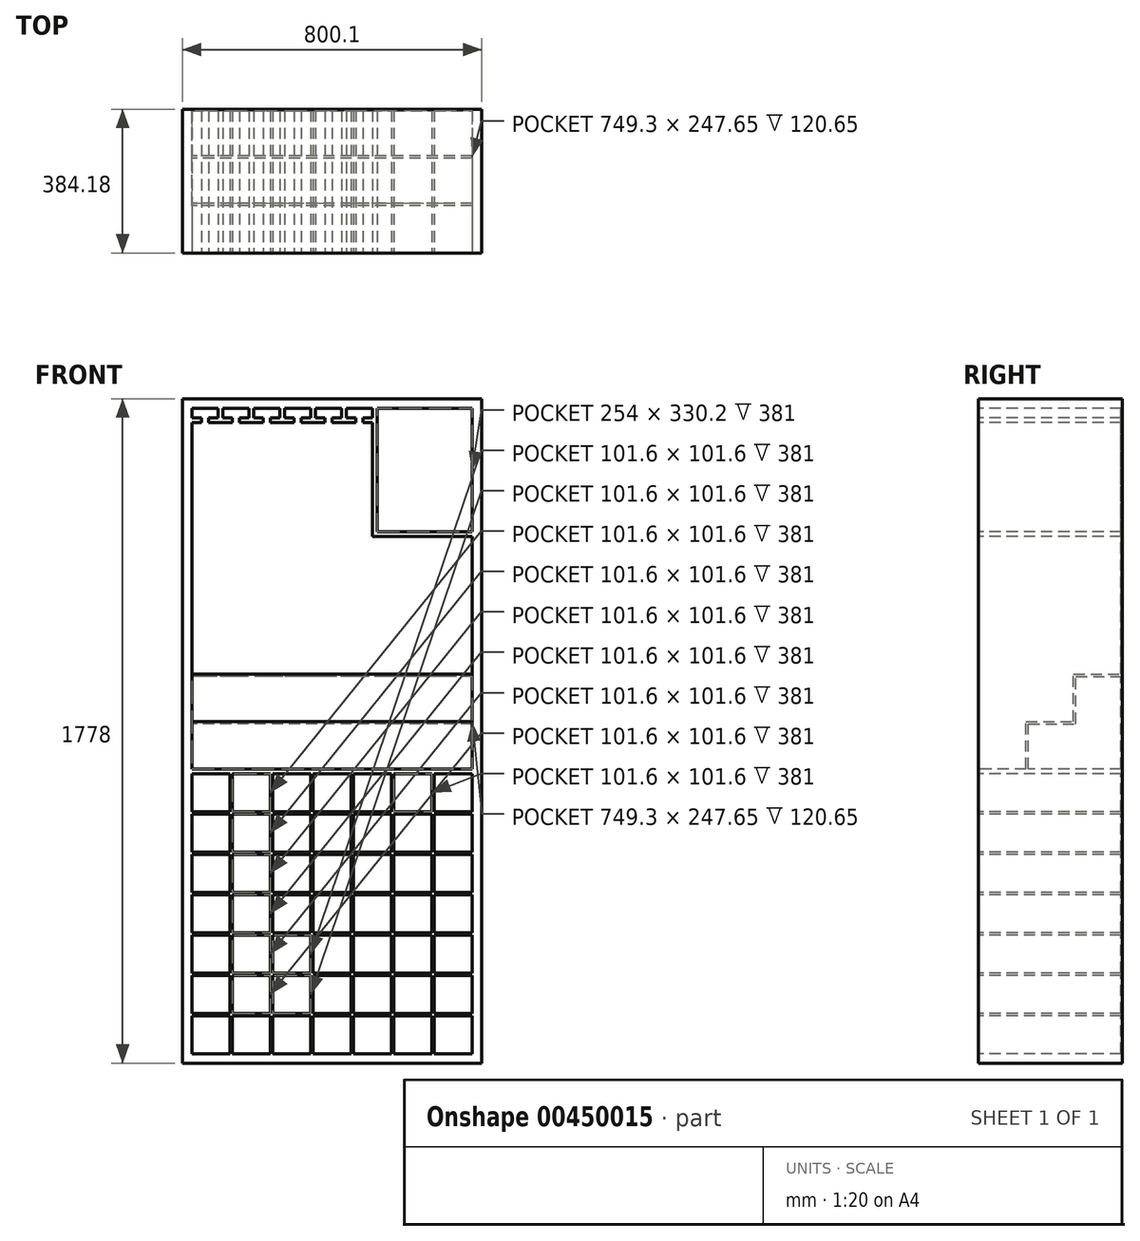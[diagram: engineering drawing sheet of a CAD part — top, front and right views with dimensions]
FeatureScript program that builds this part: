
annotation { "Feature Type Name" : "Feature", "Feature Type Description" : "" }
export const myFeature = defineFeature(function(context is Context, id is Id, definition is map)
    precondition{}
    {
        {
            var Q0;
            Q0=qCreatedBy(makeId("Front.planeOp"),FACE);
            var sketch = newSketch(context, id + "F0", { "sketchPlane" : qUnion([Q0])});
            skLineSegment(sketch, "E0", {"start": v(-400.05, 0) * mm, "end": v(400.05, 0) * mm});
            skLineSegment(sketch, "E1", {"start": v(-400.05, 0) * mm, "end": v(-400.05, 1778) * mm});
            skLineSegment(sketch, "E2", {"start": v(-400.05, 1778) * mm, "end": v(400.05, 1778) * mm});
            skLineSegment(sketch, "E3", {"start": v(400.05, 1778) * mm, "end": v(400.05, 0) * mm});
            skLineSegment(sketch, "E4.0", {"start": v(-374.65, 1752.6) * mm, "end": v(374.65, 1752.6) * mm});
            skLineSegment(sketch, "E5.0", {"start": v(-374.65, 25.4) * mm, "end": v(-374.65, 1752.6) * mm});
            skLineSegment(sketch, "E5.1", {"start": v(-374.65, 25.4) * mm, "end": v(374.65, 25.4) * mm});
            skLineSegment(sketch, "E5.2", {"start": v(374.65, 1752.6) * mm, "end": v(374.65, 25.4) * mm});
            skSolve(sketch);
        }
        {
            var Q0;
            Q0 = qSketchRegion(id + "F0", true);
            extrude(context, id + "F1", {"entities" : qUnion([Q0]), "oppositeDirection" : true, "depth" : 381 * mm});
        }
        {
            var Q0;
            Q0=makeQuery(id+"F1.opExtrude","CAP_FACE",FACE,{"disambiguationData":[OSD([sQuery(id+"F0.wireOp",EDGE,"E0"),sQuery(id+"F0.wireOp",EDGE,"E1"),sQuery(id+"F0.wireOp",EDGE,"E2"),sQuery(id+"F0.wireOp",EDGE,"E3"),sQuery(id+"F0.wireOp",EDGE,"E4.0"),sQuery(id+"F0.wireOp",EDGE,"E5.0"),sQuery(id+"F0.wireOp",EDGE,"E5.1"),sQuery(id+"F0.wireOp",EDGE,"E5.2")])],"isStart":false});
            var sketch = newSketch(context, id + "F2", { "sketchPlane" : qUnion([Q0])});
            skLineSegment(sketch, "E6.0", {"start": v(400.05, 1778) * mm, "end": v(-400.05, 1778) * mm});
            skLineSegment(sketch, "E6.1", {"start": v(-400.05, 1778) * mm, "end": v(-400.05, 0) * mm});
            skLineSegment(sketch, "E6.2", {"start": v(400.05, 0) * mm, "end": v(400.05, 1778) * mm});
            skLineSegment(sketch, "E7.0", {"start": v(400.05, 0) * mm, "end": v(-400.05, 0) * mm});
            skSolve(sketch);
        }
        {
            var Q0;
            Q0 = qSketchRegion(id + "F2", true);
            extrude(context, id + "F3", {"entities" : qUnion([Q0]), "operationType" : NewBodyOperationType.ADD, "depth" : 3.17 * mm});
        }
        {
            var Q0;
            Q0=makeQuery(id+"F1.opExtrude","CAP_FACE",FACE,{"disambiguationData":[OSD([sQuery(id+"F0.wireOp",EDGE,"E0"),sQuery(id+"F0.wireOp",EDGE,"E1"),sQuery(id+"F0.wireOp",EDGE,"E2"),sQuery(id+"F0.wireOp",EDGE,"E3"),sQuery(id+"F0.wireOp",EDGE,"E4.0"),sQuery(id+"F0.wireOp",EDGE,"E5.0"),sQuery(id+"F0.wireOp",EDGE,"E5.1"),sQuery(id+"F0.wireOp",EDGE,"E5.2")])],"isStart":true});
            var sketch = newSketch(context, id + "F4", { "sketchPlane" : qUnion([Q0])});
            skLineSegment(sketch, "E8", {"start": v(-374.65, 889) * mm, "end": v(374.65, 889) * mm, "construction": true});
            skLineSegment(sketch, "E9", {"start": v(-374.65, 774.7) * mm, "end": v(374.65, 774.7) * mm});
            skLineSegment(sketch, "E10", {"start": v(-374.65, 774.7) * mm, "end": v(-374.65, 25.4) * mm});
            skLineSegment(sketch, "E11", {"start": v(-374.65, 25.4) * mm, "end": v(374.65, 25.4) * mm});
            skLineSegment(sketch, "E12", {"start": v(374.65, 25.4) * mm, "end": v(374.65, 774.7) * mm});
            skLineSegment(sketch, "E13", {"start": v(-266.7, 774.7) * mm, "end": v(-266.7, 25.4) * mm});
            skLineSegment(sketch, "E14.0", {"start": v(-273.05, 774.7) * mm, "end": v(-273.05, 25.4) * mm});
            skLineSegment(sketch, "E15.1.0.0", {"start": v(-165.1, 774.7) * mm, "end": v(-165.1, 25.4) * mm});
            skLineSegment(sketch, "E15.1.0.1", {"start": v(-158.75, 774.7) * mm, "end": v(-158.75, 25.4) * mm});
            skLineSegment(sketch, "E15.2.0.0", {"start": v(-57.15, 774.7) * mm, "end": v(-57.15, 25.4) * mm});
            skLineSegment(sketch, "E15.2.0.1", {"start": v(-50.8, 774.7) * mm, "end": v(-50.8, 25.4) * mm});
            skLineSegment(sketch, "E15.3.0.0", {"start": v(50.8, 774.7) * mm, "end": v(50.8, 25.4) * mm});
            skLineSegment(sketch, "E15.3.0.1", {"start": v(57.15, 774.7) * mm, "end": v(57.15, 25.4) * mm});
            skLineSegment(sketch, "E15.4.0.0", {"start": v(158.75, 774.7) * mm, "end": v(158.75, 25.4) * mm});
            skLineSegment(sketch, "E15.4.0.1", {"start": v(165.1, 774.7) * mm, "end": v(165.1, 25.4) * mm});
            skLineSegment(sketch, "E15.5.0.0", {"start": v(266.7, 774.7) * mm, "end": v(266.7, 25.4) * mm});
            skLineSegment(sketch, "E15.5.0.1", {"start": v(273.05, 774.7) * mm, "end": v(273.05, 25.4) * mm});
            skLineSegment(sketch, "E15.direction1", {"start": v(-273.05, 25.4) * mm, "end": v(-165.1, 25.4) * mm, "construction": true});
            skLineSegment(sketch, "E16", {"start": v(-374.65, 127) * mm, "end": v(-273.05, 127) * mm});
            skLineSegment(sketch, "E17", {"start": v(-266.7, 127) * mm, "end": v(-165.1, 127) * mm});
            skLineSegment(sketch, "E18.trimOffspring", {"start": v(-158.75, 127) * mm, "end": v(-57.15, 127) * mm});
            skLineSegment(sketch, "E19.trimOffspring", {"start": v(-50.8, 127) * mm, "end": v(50.8, 127) * mm});
            skLineSegment(sketch, "E20.trimOffspring", {"start": v(57.15, 127) * mm, "end": v(158.75, 127) * mm});
            skLineSegment(sketch, "E21.trimOffspring", {"start": v(165.1, 127) * mm, "end": v(266.7, 127) * mm});
            skLineSegment(sketch, "E22.trimOffspring", {"start": v(273.05, 127) * mm, "end": v(374.65, 127) * mm});
            skLineSegment(sketch, "E23", {"start": v(-374.65, 133.35) * mm, "end": v(-273.05, 133.35) * mm});
            skLineSegment(sketch, "E24.trimOffspring", {"start": v(-266.7, 133.35) * mm, "end": v(-165.1, 133.35) * mm});
            skLineSegment(sketch, "E25.trimOffspring", {"start": v(-158.75, 133.35) * mm, "end": v(-57.15, 133.35) * mm});
            skLineSegment(sketch, "E26.trimOffspring", {"start": v(-50.8, 133.35) * mm, "end": v(50.8, 133.35) * mm});
            skLineSegment(sketch, "E27.trimOffspring", {"start": v(57.15, 133.35) * mm, "end": v(158.75, 133.35) * mm});
            skLineSegment(sketch, "E28.trimOffspring", {"start": v(165.1, 133.35) * mm, "end": v(266.7, 133.35) * mm});
            skLineSegment(sketch, "E29.trimOffspring", {"start": v(273.05, 133.35) * mm, "end": v(374.65, 133.35) * mm});
            skLineSegment(sketch, "E30.0.1.0", {"start": v(-374.65, 241.3) * mm, "end": v(-273.05, 241.3) * mm});
            skLineSegment(sketch, "E30.0.1.1", {"start": v(-374.65, 234.95) * mm, "end": v(-273.05, 234.95) * mm});
            skLineSegment(sketch, "E30.0.1.2", {"start": v(-266.7, 234.95) * mm, "end": v(-165.1, 234.95) * mm});
            skLineSegment(sketch, "E30.0.1.3", {"start": v(-266.7, 241.3) * mm, "end": v(-165.1, 241.3) * mm});
            skLineSegment(sketch, "E30.0.1.4", {"start": v(-158.75, 241.3) * mm, "end": v(-57.15, 241.3) * mm});
            skLineSegment(sketch, "E30.0.1.5", {"start": v(-158.75, 234.95) * mm, "end": v(-57.15, 234.95) * mm});
            skLineSegment(sketch, "E30.0.1.6", {"start": v(-50.8, 234.95) * mm, "end": v(50.8, 234.95) * mm});
            skLineSegment(sketch, "E30.0.1.7", {"start": v(-50.8, 241.3) * mm, "end": v(50.8, 241.3) * mm});
            skLineSegment(sketch, "E30.0.1.8", {"start": v(57.15, 241.3) * mm, "end": v(158.75, 241.3) * mm});
            skLineSegment(sketch, "E30.0.1.9", {"start": v(57.15, 234.95) * mm, "end": v(158.75, 234.95) * mm});
            skLineSegment(sketch, "E30.0.1.10", {"start": v(165.1, 234.95) * mm, "end": v(266.7, 234.95) * mm});
            skLineSegment(sketch, "E30.0.1.11", {"start": v(165.1, 241.3) * mm, "end": v(266.7, 241.3) * mm});
            skLineSegment(sketch, "E30.0.1.12", {"start": v(273.05, 241.3) * mm, "end": v(374.65, 241.3) * mm});
            skLineSegment(sketch, "E30.0.1.13", {"start": v(273.05, 234.95) * mm, "end": v(374.65, 234.95) * mm});
            skLineSegment(sketch, "E30.0.2.0", {"start": v(-374.65, 349.25) * mm, "end": v(-273.05, 349.25) * mm});
            skLineSegment(sketch, "E30.0.2.1", {"start": v(-374.65, 342.9) * mm, "end": v(-273.05, 342.9) * mm});
            skLineSegment(sketch, "E30.0.2.2", {"start": v(-266.7, 342.9) * mm, "end": v(-165.1, 342.9) * mm});
            skLineSegment(sketch, "E30.0.2.3", {"start": v(-266.7, 349.25) * mm, "end": v(-165.1, 349.25) * mm});
            skLineSegment(sketch, "E30.0.2.4", {"start": v(-158.75, 349.25) * mm, "end": v(-57.15, 349.25) * mm});
            skLineSegment(sketch, "E30.0.2.5", {"start": v(-158.75, 342.9) * mm, "end": v(-57.15, 342.9) * mm});
            skLineSegment(sketch, "E30.0.2.6", {"start": v(-50.8, 342.9) * mm, "end": v(50.8, 342.9) * mm});
            skLineSegment(sketch, "E30.0.2.7", {"start": v(-50.8, 349.25) * mm, "end": v(50.8, 349.25) * mm});
            skLineSegment(sketch, "E30.0.2.8", {"start": v(57.15, 349.25) * mm, "end": v(158.75, 349.25) * mm});
            skLineSegment(sketch, "E30.0.2.9", {"start": v(57.15, 342.9) * mm, "end": v(158.75, 342.9) * mm});
            skLineSegment(sketch, "E30.0.2.10", {"start": v(165.1, 342.9) * mm, "end": v(266.7, 342.9) * mm});
            skLineSegment(sketch, "E30.0.2.11", {"start": v(165.1, 349.25) * mm, "end": v(266.7, 349.25) * mm});
            skLineSegment(sketch, "E30.0.2.12", {"start": v(273.05, 349.25) * mm, "end": v(374.65, 349.25) * mm});
            skLineSegment(sketch, "E30.0.2.13", {"start": v(273.05, 342.9) * mm, "end": v(374.65, 342.9) * mm});
            skLineSegment(sketch, "E30.0.3.0", {"start": v(-374.65, 457.2) * mm, "end": v(-273.05, 457.2) * mm});
            skLineSegment(sketch, "E30.0.3.1", {"start": v(-374.65, 450.85) * mm, "end": v(-273.05, 450.85) * mm});
            skLineSegment(sketch, "E30.0.3.2", {"start": v(-266.7, 450.85) * mm, "end": v(-165.1, 450.85) * mm});
            skLineSegment(sketch, "E30.0.3.3", {"start": v(-266.7, 457.2) * mm, "end": v(-165.1, 457.2) * mm});
            skLineSegment(sketch, "E30.0.3.4", {"start": v(-158.75, 457.2) * mm, "end": v(-57.15, 457.2) * mm});
            skLineSegment(sketch, "E30.0.3.5", {"start": v(-158.75, 450.85) * mm, "end": v(-57.15, 450.85) * mm});
            skLineSegment(sketch, "E30.0.3.6", {"start": v(-50.8, 450.85) * mm, "end": v(50.8, 450.85) * mm});
            skLineSegment(sketch, "E30.0.3.7", {"start": v(-50.8, 457.2) * mm, "end": v(50.8, 457.2) * mm});
            skLineSegment(sketch, "E30.0.3.8", {"start": v(57.15, 457.2) * mm, "end": v(158.75, 457.2) * mm});
            skLineSegment(sketch, "E30.0.3.9", {"start": v(57.15, 450.85) * mm, "end": v(158.75, 450.85) * mm});
            skLineSegment(sketch, "E30.0.3.10", {"start": v(165.1, 450.85) * mm, "end": v(266.7, 450.85) * mm});
            skLineSegment(sketch, "E30.0.3.11", {"start": v(165.1, 457.2) * mm, "end": v(266.7, 457.2) * mm});
            skLineSegment(sketch, "E30.0.3.12", {"start": v(273.05, 457.2) * mm, "end": v(374.65, 457.2) * mm});
            skLineSegment(sketch, "E30.0.3.13", {"start": v(273.05, 450.85) * mm, "end": v(374.65, 450.85) * mm});
            skLineSegment(sketch, "E30.0.4.0", {"start": v(-374.65, 565.15) * mm, "end": v(-273.05, 565.15) * mm});
            skLineSegment(sketch, "E30.0.4.1", {"start": v(-374.65, 558.8) * mm, "end": v(-273.05, 558.8) * mm});
            skLineSegment(sketch, "E30.0.4.2", {"start": v(-266.7, 558.8) * mm, "end": v(-165.1, 558.8) * mm});
            skLineSegment(sketch, "E30.0.4.3", {"start": v(-266.7, 565.15) * mm, "end": v(-165.1, 565.15) * mm});
            skLineSegment(sketch, "E30.0.4.4", {"start": v(-158.75, 565.15) * mm, "end": v(-57.15, 565.15) * mm});
            skLineSegment(sketch, "E30.0.4.5", {"start": v(-158.75, 558.8) * mm, "end": v(-57.15, 558.8) * mm});
            skLineSegment(sketch, "E30.0.4.6", {"start": v(-50.8, 558.8) * mm, "end": v(50.8, 558.8) * mm});
            skLineSegment(sketch, "E30.0.4.7", {"start": v(-50.8, 565.15) * mm, "end": v(50.8, 565.15) * mm});
            skLineSegment(sketch, "E30.0.4.8", {"start": v(57.15, 565.15) * mm, "end": v(158.75, 565.15) * mm});
            skLineSegment(sketch, "E30.0.4.9", {"start": v(57.15, 558.8) * mm, "end": v(158.75, 558.8) * mm});
            skLineSegment(sketch, "E30.0.4.10", {"start": v(165.1, 558.8) * mm, "end": v(266.7, 558.8) * mm});
            skLineSegment(sketch, "E30.0.4.11", {"start": v(165.1, 565.15) * mm, "end": v(266.7, 565.15) * mm});
            skLineSegment(sketch, "E30.0.4.12", {"start": v(273.05, 565.15) * mm, "end": v(374.65, 565.15) * mm});
            skLineSegment(sketch, "E30.0.4.13", {"start": v(273.05, 558.8) * mm, "end": v(374.65, 558.8) * mm});
            skLineSegment(sketch, "E30.0.5.0", {"start": v(-374.65, 673.1) * mm, "end": v(-273.05, 673.1) * mm});
            skLineSegment(sketch, "E30.0.5.1", {"start": v(-374.65, 666.75) * mm, "end": v(-273.05, 666.75) * mm});
            skLineSegment(sketch, "E30.0.5.2", {"start": v(-266.7, 666.75) * mm, "end": v(-165.1, 666.75) * mm});
            skLineSegment(sketch, "E30.0.5.3", {"start": v(-266.7, 673.1) * mm, "end": v(-165.1, 673.1) * mm});
            skLineSegment(sketch, "E30.0.5.4", {"start": v(-158.75, 673.1) * mm, "end": v(-57.15, 673.1) * mm});
            skLineSegment(sketch, "E30.0.5.5", {"start": v(-158.75, 666.75) * mm, "end": v(-57.15, 666.75) * mm});
            skLineSegment(sketch, "E30.0.5.6", {"start": v(-50.8, 666.75) * mm, "end": v(50.8, 666.75) * mm});
            skLineSegment(sketch, "E30.0.5.7", {"start": v(-50.8, 673.1) * mm, "end": v(50.8, 673.1) * mm});
            skLineSegment(sketch, "E30.0.5.8", {"start": v(57.15, 673.1) * mm, "end": v(158.75, 673.1) * mm});
            skLineSegment(sketch, "E30.0.5.9", {"start": v(57.15, 666.75) * mm, "end": v(158.75, 666.75) * mm});
            skLineSegment(sketch, "E30.0.5.10", {"start": v(165.1, 666.75) * mm, "end": v(266.7, 666.75) * mm});
            skLineSegment(sketch, "E30.0.5.11", {"start": v(165.1, 673.1) * mm, "end": v(266.7, 673.1) * mm});
            skLineSegment(sketch, "E30.0.5.12", {"start": v(273.05, 673.1) * mm, "end": v(374.65, 673.1) * mm});
            skLineSegment(sketch, "E30.0.5.13", {"start": v(273.05, 666.75) * mm, "end": v(374.65, 666.75) * mm});
            skLineSegment(sketch, "E30.direction1", {"start": v(-374.65, 127) * mm, "end": v(-273.05, 127) * mm, "construction": true});
            skLineSegment(sketch, "E30.direction2", {"start": v(-374.65, 127) * mm, "end": v(-374.65, 234.95) * mm, "construction": true});
            skLineSegment(sketch, "E31", {"start": v(-374.65, 787.4) * mm, "end": v(374.65, 787.4) * mm});
            skSolve(sketch);
        }
        {
            var Q0;
            {var subQ0=sQuery(id+"F4.wireOp",EDGE,"E16");Q0=makeQuery(id+"F4.imprint","IMPRINT",FACE,{"disambiguationData":[TD([[makeQuery(id+"F4.imprint","IMPRINT",EDGE,{"derivedFrom":subQ0}),1.0]])]});}
            var Q1;
            {var subQ0=sQuery(id+"F4.wireOp",EDGE,"E30.0.1.0");Q1=makeQuery(id+"F4.imprint","IMPRINT",FACE,{"disambiguationData":[TD([[makeQuery(id+"F4.imprint","IMPRINT",EDGE,{"derivedFrom":subQ0}),-1.0]])]});}
            var Q2;
            {var subQ0=sQuery(id+"F4.wireOp",EDGE,"E30.0.2.0");Q2=makeQuery(id+"F4.imprint","IMPRINT",FACE,{"disambiguationData":[TD([[makeQuery(id+"F4.imprint","IMPRINT",EDGE,{"derivedFrom":subQ0}),-1.0]])]});}
            var Q3;
            {var subQ0=sQuery(id+"F4.wireOp",EDGE,"E30.0.3.0");Q3=makeQuery(id+"F4.imprint","IMPRINT",FACE,{"disambiguationData":[TD([[makeQuery(id+"F4.imprint","IMPRINT",EDGE,{"derivedFrom":subQ0}),-1.0]])]});}
            var Q4;
            {var subQ0=sQuery(id+"F4.wireOp",EDGE,"E30.0.4.0");Q4=makeQuery(id+"F4.imprint","IMPRINT",FACE,{"disambiguationData":[TD([[makeQuery(id+"F4.imprint","IMPRINT",EDGE,{"derivedFrom":subQ0}),-1.0]])]});}
            var Q5;
            {var subQ0=sQuery(id+"F4.wireOp",EDGE,"E30.0.5.0");Q5=makeQuery(id+"F4.imprint","IMPRINT",FACE,{"disambiguationData":[TD([[makeQuery(id+"F4.imprint","IMPRINT",EDGE,{"derivedFrom":subQ0}),-1.0]])]});}
            var Q6;
            {var subQ0=sQuery(id+"F4.wireOp",EDGE,"E30.0.5.12");Q6=makeQuery(id+"F4.imprint","IMPRINT",FACE,{"disambiguationData":[TD([[makeQuery(id+"F4.imprint","IMPRINT",EDGE,{"derivedFrom":subQ0}),-1.0]])]});}
            var Q7;
            {var subQ0=sQuery(id+"F4.wireOp",EDGE,"E30.0.4.12");Q7=makeQuery(id+"F4.imprint","IMPRINT",FACE,{"disambiguationData":[TD([[makeQuery(id+"F4.imprint","IMPRINT",EDGE,{"derivedFrom":subQ0}),-1.0]])]});}
            var Q8;
            {var subQ0=sQuery(id+"F4.wireOp",EDGE,"E30.0.3.12");Q8=makeQuery(id+"F4.imprint","IMPRINT",FACE,{"disambiguationData":[TD([[makeQuery(id+"F4.imprint","IMPRINT",EDGE,{"derivedFrom":subQ0}),-1.0]])]});}
            var Q9;
            {var subQ0=sQuery(id+"F4.wireOp",EDGE,"E30.0.2.12");Q9=makeQuery(id+"F4.imprint","IMPRINT",FACE,{"disambiguationData":[TD([[makeQuery(id+"F4.imprint","IMPRINT",EDGE,{"derivedFrom":subQ0}),-1.0]])]});}
            var Q10;
            {var subQ0=sQuery(id+"F4.wireOp",EDGE,"E30.0.1.12");Q10=makeQuery(id+"F4.imprint","IMPRINT",FACE,{"disambiguationData":[TD([[makeQuery(id+"F4.imprint","IMPRINT",EDGE,{"derivedFrom":subQ0}),-1.0]])]});}
            var Q11;
            {var subQ0=sQuery(id+"F4.wireOp",EDGE,"E22.trimOffspring");Q11=makeQuery(id+"F4.imprint","IMPRINT",FACE,{"disambiguationData":[TD([[makeQuery(id+"F4.imprint","IMPRINT",EDGE,{"derivedFrom":subQ0}),1.0]])]});}
            var Q12;
            {var subQ8=sQuery(id+"F4.wireOp",EDGE,"E9");var subQ10=sQuery(id+"F4.wireOp",EDGE,"E13");var subQ20=makeQuery(id+"F4.imprint","INTERSECT",VERTEX,{"derivedFrom":[subQ8,subQ10]});Q12=makeQuery(id+"F4.imprint","IMPRINT",FACE,{"disambiguationData":[TD([[makeQuery(id+"F4.imprint","IMPRINT",EDGE,{"disambiguationData":[TD([[subQ20,1.0]])],"derivedFrom":subQ8}),-1.0]])]});}
            var Q13;
            {var subQ3=sQuery(id+"F4.wireOp",EDGE,"E15.1.0.0");var subQ4=sQuery(id+"F4.wireOp",EDGE,"E9");var subQ5=makeQuery(id+"F4.imprint","INTERSECT",VERTEX,{"derivedFrom":[subQ4,subQ3]});Q13=makeQuery(id+"F4.imprint","IMPRINT",FACE,{"disambiguationData":[TD([[makeQuery(id+"F4.imprint","IMPRINT",EDGE,{"disambiguationData":[TD([[subQ5,-1.0]])],"derivedFrom":subQ4}),-1.0]])]});}
            var Q14;
            {var subQ7=sQuery(id+"F4.wireOp",EDGE,"E9");var subQ9=sQuery(id+"F4.wireOp",EDGE,"E15.2.0.0");var subQ17=makeQuery(id+"F4.imprint","INTERSECT",VERTEX,{"derivedFrom":[subQ7,subQ9]});Q14=makeQuery(id+"F4.imprint","IMPRINT",FACE,{"disambiguationData":[TD([[makeQuery(id+"F4.imprint","IMPRINT",EDGE,{"disambiguationData":[TD([[subQ17,-1.0]])],"derivedFrom":subQ7}),-1.0]])]});}
            var Q15;
            {var subQ8=sQuery(id+"F4.wireOp",EDGE,"E9");var subQ10=sQuery(id+"F4.wireOp",EDGE,"E15.3.0.0");var subQ20=makeQuery(id+"F4.imprint","INTERSECT",VERTEX,{"derivedFrom":[subQ8,subQ10]});Q15=makeQuery(id+"F4.imprint","IMPRINT",FACE,{"disambiguationData":[TD([[makeQuery(id+"F4.imprint","IMPRINT",EDGE,{"disambiguationData":[TD([[subQ20,-1.0]])],"derivedFrom":subQ8}),-1.0]])]});}
            var Q16;
            {var subQ7=sQuery(id+"F4.wireOp",EDGE,"E9");var subQ10=sQuery(id+"F4.wireOp",EDGE,"E15.4.0.0");var subQ20=makeQuery(id+"F4.imprint","INTERSECT",VERTEX,{"derivedFrom":[subQ7,subQ10]});Q16=makeQuery(id+"F4.imprint","IMPRINT",FACE,{"disambiguationData":[TD([[makeQuery(id+"F4.imprint","IMPRINT",EDGE,{"disambiguationData":[TD([[subQ20,-1.0]])],"derivedFrom":subQ7}),-1.0]])]});}
            var Q17;
            {var subQ5=sQuery(id+"F4.wireOp",EDGE,"E15.5.0.0");var subQ6=sQuery(id+"F4.wireOp",EDGE,"E9");var subQ7=makeQuery(id+"F4.imprint","INTERSECT",VERTEX,{"derivedFrom":[subQ6,subQ5]});Q17=makeQuery(id+"F4.imprint","IMPRINT",FACE,{"disambiguationData":[TD([[makeQuery(id+"F4.imprint","IMPRINT",EDGE,{"disambiguationData":[TD([[subQ7,-1.0]])],"derivedFrom":subQ6}),-1.0]])]});}
            var Q18;
            {var subQ0=sQuery(id+"F4.wireOp",EDGE,"E30.0.5.2");Q18=makeQuery(id+"F4.imprint","IMPRINT",FACE,{"disambiguationData":[TD([[makeQuery(id+"F4.imprint","IMPRINT",EDGE,{"derivedFrom":subQ0}),1.0]])]});}
            var Q19;
            {var subQ0=sQuery(id+"F4.wireOp",EDGE,"E30.0.5.4");Q19=makeQuery(id+"F4.imprint","IMPRINT",FACE,{"disambiguationData":[TD([[makeQuery(id+"F4.imprint","IMPRINT",EDGE,{"derivedFrom":subQ0}),-1.0]])]});}
            var Q20;
            {var subQ0=sQuery(id+"F4.wireOp",EDGE,"E30.0.4.2");Q20=makeQuery(id+"F4.imprint","IMPRINT",FACE,{"disambiguationData":[TD([[makeQuery(id+"F4.imprint","IMPRINT",EDGE,{"derivedFrom":subQ0}),1.0]])]});}
            var Q21;
            {var subQ0=sQuery(id+"F4.wireOp",EDGE,"E30.0.3.2");Q21=makeQuery(id+"F4.imprint","IMPRINT",FACE,{"disambiguationData":[TD([[makeQuery(id+"F4.imprint","IMPRINT",EDGE,{"derivedFrom":subQ0}),1.0]])]});}
            var Q22;
            {var subQ0=sQuery(id+"F4.wireOp",EDGE,"E30.0.3.4");Q22=makeQuery(id+"F4.imprint","IMPRINT",FACE,{"disambiguationData":[TD([[makeQuery(id+"F4.imprint","IMPRINT",EDGE,{"derivedFrom":subQ0}),-1.0]])]});}
            var Q23;
            {var subQ0=sQuery(id+"F4.wireOp",EDGE,"E30.0.4.4");Q23=makeQuery(id+"F4.imprint","IMPRINT",FACE,{"disambiguationData":[TD([[makeQuery(id+"F4.imprint","IMPRINT",EDGE,{"derivedFrom":subQ0}),-1.0]])]});}
            var Q24;
            {var subQ0=sQuery(id+"F4.wireOp",EDGE,"E30.0.4.6");Q24=makeQuery(id+"F4.imprint","IMPRINT",FACE,{"disambiguationData":[TD([[makeQuery(id+"F4.imprint","IMPRINT",EDGE,{"derivedFrom":subQ0}),1.0]])]});}
            var Q25;
            {var subQ0=sQuery(id+"F4.wireOp",EDGE,"E30.0.5.6");Q25=makeQuery(id+"F4.imprint","IMPRINT",FACE,{"disambiguationData":[TD([[makeQuery(id+"F4.imprint","IMPRINT",EDGE,{"derivedFrom":subQ0}),1.0]])]});}
            var Q26;
            {var subQ0=sQuery(id+"F4.wireOp",EDGE,"E30.0.5.8");Q26=makeQuery(id+"F4.imprint","IMPRINT",FACE,{"disambiguationData":[TD([[makeQuery(id+"F4.imprint","IMPRINT",EDGE,{"derivedFrom":subQ0}),-1.0]])]});}
            var Q27;
            {var subQ0=sQuery(id+"F4.wireOp",EDGE,"E30.0.4.8");Q27=makeQuery(id+"F4.imprint","IMPRINT",FACE,{"disambiguationData":[TD([[makeQuery(id+"F4.imprint","IMPRINT",EDGE,{"derivedFrom":subQ0}),-1.0]])]});}
            var Q28;
            {var subQ0=sQuery(id+"F4.wireOp",EDGE,"E30.0.2.2");Q28=makeQuery(id+"F4.imprint","IMPRINT",FACE,{"disambiguationData":[TD([[makeQuery(id+"F4.imprint","IMPRINT",EDGE,{"derivedFrom":subQ0}),1.0]])]});}
            var Q29;
            {var subQ0=sQuery(id+"F4.wireOp",EDGE,"E30.0.1.2");Q29=makeQuery(id+"F4.imprint","IMPRINT",FACE,{"disambiguationData":[TD([[makeQuery(id+"F4.imprint","IMPRINT",EDGE,{"derivedFrom":subQ0}),1.0]])]});}
            var Q30;
            {var subQ0=sQuery(id+"F4.wireOp",EDGE,"E17");Q30=makeQuery(id+"F4.imprint","IMPRINT",FACE,{"disambiguationData":[TD([[makeQuery(id+"F4.imprint","IMPRINT",EDGE,{"derivedFrom":subQ0}),1.0]])]});}
            var Q31;
            {var subQ0=sQuery(id+"F4.wireOp",EDGE,"E18.trimOffspring");Q31=makeQuery(id+"F4.imprint","IMPRINT",FACE,{"disambiguationData":[TD([[makeQuery(id+"F4.imprint","IMPRINT",EDGE,{"derivedFrom":subQ0}),1.0]])]});}
            var Q32;
            {var subQ0=sQuery(id+"F4.wireOp",EDGE,"E30.0.1.4");Q32=makeQuery(id+"F4.imprint","IMPRINT",FACE,{"disambiguationData":[TD([[makeQuery(id+"F4.imprint","IMPRINT",EDGE,{"derivedFrom":subQ0}),-1.0]])]});}
            var Q33;
            {var subQ0=sQuery(id+"F4.wireOp",EDGE,"E30.0.2.4");Q33=makeQuery(id+"F4.imprint","IMPRINT",FACE,{"disambiguationData":[TD([[makeQuery(id+"F4.imprint","IMPRINT",EDGE,{"derivedFrom":subQ0}),-1.0]])]});}
            var Q34;
            {var subQ0=sQuery(id+"F4.wireOp",EDGE,"E30.0.2.6");Q34=makeQuery(id+"F4.imprint","IMPRINT",FACE,{"disambiguationData":[TD([[makeQuery(id+"F4.imprint","IMPRINT",EDGE,{"derivedFrom":subQ0}),1.0]])]});}
            var Q35;
            {var subQ0=sQuery(id+"F4.wireOp",EDGE,"E30.0.2.8");Q35=makeQuery(id+"F4.imprint","IMPRINT",FACE,{"disambiguationData":[TD([[makeQuery(id+"F4.imprint","IMPRINT",EDGE,{"derivedFrom":subQ0}),-1.0]])]});}
            var Q36;
            {var subQ0=sQuery(id+"F4.wireOp",EDGE,"E30.0.1.6");Q36=makeQuery(id+"F4.imprint","IMPRINT",FACE,{"disambiguationData":[TD([[makeQuery(id+"F4.imprint","IMPRINT",EDGE,{"derivedFrom":subQ0}),1.0]])]});}
            var Q37;
            {var subQ0=sQuery(id+"F4.wireOp",EDGE,"E19.trimOffspring");Q37=makeQuery(id+"F4.imprint","IMPRINT",FACE,{"disambiguationData":[TD([[makeQuery(id+"F4.imprint","IMPRINT",EDGE,{"derivedFrom":subQ0}),1.0]])]});}
            var Q38;
            {var subQ0=sQuery(id+"F4.wireOp",EDGE,"E20.trimOffspring");Q38=makeQuery(id+"F4.imprint","IMPRINT",FACE,{"disambiguationData":[TD([[makeQuery(id+"F4.imprint","IMPRINT",EDGE,{"derivedFrom":subQ0}),1.0]])]});}
            var Q39;
            {var subQ0=sQuery(id+"F4.wireOp",EDGE,"E21.trimOffspring");Q39=makeQuery(id+"F4.imprint","IMPRINT",FACE,{"disambiguationData":[TD([[makeQuery(id+"F4.imprint","IMPRINT",EDGE,{"derivedFrom":subQ0}),1.0]])]});}
            var Q40;
            {var subQ0=sQuery(id+"F4.wireOp",EDGE,"E30.0.1.10");Q40=makeQuery(id+"F4.imprint","IMPRINT",FACE,{"disambiguationData":[TD([[makeQuery(id+"F4.imprint","IMPRINT",EDGE,{"derivedFrom":subQ0}),1.0]])]});}
            var Q41;
            {var subQ0=sQuery(id+"F4.wireOp",EDGE,"E30.0.1.8");Q41=makeQuery(id+"F4.imprint","IMPRINT",FACE,{"disambiguationData":[TD([[makeQuery(id+"F4.imprint","IMPRINT",EDGE,{"derivedFrom":subQ0}),-1.0]])]});}
            var Q42;
            {var subQ0=sQuery(id+"F4.wireOp",EDGE,"E30.0.2.10");Q42=makeQuery(id+"F4.imprint","IMPRINT",FACE,{"disambiguationData":[TD([[makeQuery(id+"F4.imprint","IMPRINT",EDGE,{"derivedFrom":subQ0}),1.0]])]});}
            var Q43;
            {var subQ0=sQuery(id+"F4.wireOp",EDGE,"E30.0.3.10");Q43=makeQuery(id+"F4.imprint","IMPRINT",FACE,{"disambiguationData":[TD([[makeQuery(id+"F4.imprint","IMPRINT",EDGE,{"derivedFrom":subQ0}),1.0]])]});}
            var Q44;
            {var subQ0=sQuery(id+"F4.wireOp",EDGE,"E30.0.3.8");Q44=makeQuery(id+"F4.imprint","IMPRINT",FACE,{"disambiguationData":[TD([[makeQuery(id+"F4.imprint","IMPRINT",EDGE,{"derivedFrom":subQ0}),-1.0]])]});}
            var Q45;
            {var subQ0=sQuery(id+"F4.wireOp",EDGE,"E30.0.3.6");Q45=makeQuery(id+"F4.imprint","IMPRINT",FACE,{"disambiguationData":[TD([[makeQuery(id+"F4.imprint","IMPRINT",EDGE,{"derivedFrom":subQ0}),1.0]])]});}
            var Q46;
            {var subQ0=sQuery(id+"F4.wireOp",EDGE,"E30.0.4.10");Q46=makeQuery(id+"F4.imprint","IMPRINT",FACE,{"disambiguationData":[TD([[makeQuery(id+"F4.imprint","IMPRINT",EDGE,{"derivedFrom":subQ0}),1.0]])]});}
            var Q47;
            {var subQ0=sQuery(id+"F4.wireOp",EDGE,"E30.0.5.10");Q47=makeQuery(id+"F4.imprint","IMPRINT",FACE,{"disambiguationData":[TD([[makeQuery(id+"F4.imprint","IMPRINT",EDGE,{"derivedFrom":subQ0}),1.0]])]});}
            var Q48;
            {var subQ11=sQuery(id+"F4.wireOp",EDGE,"E31");Q48=makeQuery(id+"F4.imprint","IMPRINT",FACE,{"disambiguationData":[TD([[makeQuery(id+"F4.imprint","IMPRINT",EDGE,{"derivedFrom":subQ11}),-1.0]])]});}
            var Q49;
            Q49=makeQuery(id+"F3.opExtrude","CAP_FACE",FACE,{"disambiguationData":[OSD([sQuery(id+"F2.wireOp",EDGE,"E6.0"),sQuery(id+"F2.wireOp",EDGE,"E6.1"),sQuery(id+"F2.wireOp",EDGE,"E6.2"),sQuery(id+"F2.wireOp",EDGE,"E7.0")])],"isStart":true});
            extrude(context, id + "F5", {"entities" : qUnion([Q0, Q1, Q2, Q3, Q4, Q5, Q6, Q7, Q8, Q9, Q10, Q11, Q12, Q13, Q14, Q15, Q16, Q17, Q18, Q19, Q20, Q21, Q22, Q23, Q24, Q25, Q26, Q27, Q28, Q29, Q30, Q31, Q32, Q33, Q34, Q35, Q36, Q37, Q38, Q39, Q40, Q41, Q42, Q43, Q44, Q45, Q46, Q47, Q48]), "operationType" : NewBodyOperationType.ADD, "endBound" : BoundingType.UP_TO_SURFACE, "oppositeDirection" : true, "endBoundEntityFace" : qUnion([Q49]), "depth" : 256.54 * mm});
        }
        {
            var Q0;
            {var subQ2=sQuery(id+"F0.wireOp",EDGE,"E5.0");var subQ3=sQuery(id+"F0.wireOp",EDGE,"E4.0");Q0=makeQuery(id+"F5.boolean.opBoolean","SPLIT",FACE,{"disambiguationData":[TD([makeQuery(id+"F1.opExtrude","SWEPT_FACE",FACE,{"disambiguationData":[OSD([subQ3])]})])],"derivedFrom":makeQuery(id+"F1.opExtrude","SWEPT_FACE",FACE,{"disambiguationData":[OSD([subQ2])]})});}
            var sketch = newSketch(context, id + "F6", { "sketchPlane" : qUnion([Q0])});
            skPoint(sketch, "E32.0", {"position": v(0, 787.4) * mm});
            skLineSegment(sketch, "E33", {"start": v(0, 787.4) * mm, "end": v(381, 787.4) * mm, "construction": true});
            skLineSegment(sketch, "E34", {"start": v(127, 787.4) * mm, "end": v(127, 914.4) * mm});
            skLineSegment(sketch, "E35", {"start": v(127, 914.4) * mm, "end": v(254, 914.4) * mm});
            skLineSegment(sketch, "E36", {"start": v(254, 914.4) * mm, "end": v(254, 1041.4) * mm});
            skLineSegment(sketch, "E37", {"start": v(254, 1041.4) * mm, "end": v(381, 1041.4) * mm});
            skLineSegment(sketch, "E38.0", {"start": v(260.35, 1035.05) * mm, "end": v(381, 1035.05) * mm});
            skLineSegment(sketch, "E38.1", {"start": v(260.35, 908.05) * mm, "end": v(260.35, 1035.05) * mm});
            skLineSegment(sketch, "E38.2", {"start": v(133.35, 908.05) * mm, "end": v(260.35, 908.05) * mm});
            skLineSegment(sketch, "E38.3", {"start": v(133.35, 787.4) * mm, "end": v(133.35, 908.05) * mm});
            skLineSegment(sketch, "E39", {"start": v(127, 787.4) * mm, "end": v(133.35, 787.4) * mm});
            skLineSegment(sketch, "E40", {"start": v(381, 1041.4) * mm, "end": v(381, 1035.05) * mm});
            skSolve(sketch);
        }
        {
            var Q0;
            Q0 = qSketchRegion(id + "F6", true);
            extrude(context, id + "F7", {"entities" : qUnion([Q0]), "operationType" : NewBodyOperationType.ADD, "endBound" : BoundingType.UP_TO_NEXT, "depth" : 330.2 * mm});
        }
        {
            var Q0;
            {var subQ0=sQuery(id+"F0.wireOp",EDGE,"E5.2");var subQ1=sQuery(id+"F0.wireOp",EDGE,"E5.0");Q0=makeQuery(id+"F5.boolean.opBoolean","MERGE",FACE,{"derivedFrom":[makeQuery(id+"F1.opExtrude","CAP_FACE",FACE,{"disambiguationData":[OSD([sQuery(id+"F0.wireOp",EDGE,"E0"),sQuery(id+"F0.wireOp",EDGE,"E1"),sQuery(id+"F0.wireOp",EDGE,"E2"),sQuery(id+"F0.wireOp",EDGE,"E3"),sQuery(id+"F0.wireOp",EDGE,"E4.0"),subQ1,sQuery(id+"F0.wireOp",EDGE,"E5.1"),subQ0])],"isStart":true}),makeQuery(id+"F5.opExtrude","CAP_FACE",FACE,{"disambiguationData":[OSD([subQ1,subQ0,sQuery(id+"F4.wireOp",EDGE,"E9"),sQuery(id+"F4.wireOp",EDGE,"E10"),sQuery(id+"F4.wireOp",EDGE,"E11"),sQuery(id+"F4.wireOp",EDGE,"E12"),sQuery(id+"F4.wireOp",EDGE,"E13"),sQuery(id+"F4.wireOp",EDGE,"E14.0"),sQuery(id+"F4.wireOp",EDGE,"E15.1.0.0"),sQuery(id+"F4.wireOp",EDGE,"E15.1.0.1"),sQuery(id+"F4.wireOp",EDGE,"E15.2.0.0"),sQuery(id+"F4.wireOp",EDGE,"E15.2.0.1"),sQuery(id+"F4.wireOp",EDGE,"E15.3.0.0"),sQuery(id+"F4.wireOp",EDGE,"E15.3.0.1"),sQuery(id+"F4.wireOp",EDGE,"E15.4.0.0"),sQuery(id+"F4.wireOp",EDGE,"E15.4.0.1"),sQuery(id+"F4.wireOp",EDGE,"E15.5.0.0"),sQuery(id+"F4.wireOp",EDGE,"E15.5.0.1"),sQuery(id+"F4.wireOp",EDGE,"E16"),sQuery(id+"F4.wireOp",EDGE,"E17"),sQuery(id+"F4.wireOp",EDGE,"E18.trimOffspring"),sQuery(id+"F4.wireOp",EDGE,"E19.trimOffspring"),sQuery(id+"F4.wireOp",EDGE,"E20.trimOffspring"),sQuery(id+"F4.wireOp",EDGE,"E21.trimOffspring"),sQuery(id+"F4.wireOp",EDGE,"E22.trimOffspring"),sQuery(id+"F4.wireOp",EDGE,"E23"),sQuery(id+"F4.wireOp",EDGE,"E24.trimOffspring"),sQuery(id+"F4.wireOp",EDGE,"E25.trimOffspring"),sQuery(id+"F4.wireOp",EDGE,"E26.trimOffspring"),sQuery(id+"F4.wireOp",EDGE,"E27.trimOffspring"),sQuery(id+"F4.wireOp",EDGE,"E28.trimOffspring"),sQuery(id+"F4.wireOp",EDGE,"E29.trimOffspring"),sQuery(id+"F4.wireOp",EDGE,"E30.0.1.0"),sQuery(id+"F4.wireOp",EDGE,"E30.0.1.1"),sQuery(id+"F4.wireOp",EDGE,"E30.0.1.2"),sQuery(id+"F4.wireOp",EDGE,"E30.0.1.3"),sQuery(id+"F4.wireOp",EDGE,"E30.0.1.4"),sQuery(id+"F4.wireOp",EDGE,"E30.0.1.5"),sQuery(id+"F4.wireOp",EDGE,"E30.0.1.6"),sQuery(id+"F4.wireOp",EDGE,"E30.0.1.7"),sQuery(id+"F4.wireOp",EDGE,"E30.0.1.8"),sQuery(id+"F4.wireOp",EDGE,"E30.0.1.9"),sQuery(id+"F4.wireOp",EDGE,"E30.0.1.10"),sQuery(id+"F4.wireOp",EDGE,"E30.0.1.11"),sQuery(id+"F4.wireOp",EDGE,"E30.0.1.12"),sQuery(id+"F4.wireOp",EDGE,"E30.0.1.13"),sQuery(id+"F4.wireOp",EDGE,"E30.0.2.0"),sQuery(id+"F4.wireOp",EDGE,"E30.0.2.1"),sQuery(id+"F4.wireOp",EDGE,"E30.0.2.2"),sQuery(id+"F4.wireOp",EDGE,"E30.0.2.3"),sQuery(id+"F4.wireOp",EDGE,"E30.0.2.4"),sQuery(id+"F4.wireOp",EDGE,"E30.0.2.5"),sQuery(id+"F4.wireOp",EDGE,"E30.0.2.6"),sQuery(id+"F4.wireOp",EDGE,"E30.0.2.7"),sQuery(id+"F4.wireOp",EDGE,"E30.0.2.8"),sQuery(id+"F4.wireOp",EDGE,"E30.0.2.9"),sQuery(id+"F4.wireOp",EDGE,"E30.0.2.10"),sQuery(id+"F4.wireOp",EDGE,"E30.0.2.11"),sQuery(id+"F4.wireOp",EDGE,"E30.0.2.12"),sQuery(id+"F4.wireOp",EDGE,"E30.0.2.13"),sQuery(id+"F4.wireOp",EDGE,"E30.0.3.0"),sQuery(id+"F4.wireOp",EDGE,"E30.0.3.1"),sQuery(id+"F4.wireOp",EDGE,"E30.0.3.2"),sQuery(id+"F4.wireOp",EDGE,"E30.0.3.3"),sQuery(id+"F4.wireOp",EDGE,"E30.0.3.4"),sQuery(id+"F4.wireOp",EDGE,"E30.0.3.5"),sQuery(id+"F4.wireOp",EDGE,"E30.0.3.6"),sQuery(id+"F4.wireOp",EDGE,"E30.0.3.7"),sQuery(id+"F4.wireOp",EDGE,"E30.0.3.8"),sQuery(id+"F4.wireOp",EDGE,"E30.0.3.9"),sQuery(id+"F4.wireOp",EDGE,"E30.0.3.10"),sQuery(id+"F4.wireOp",EDGE,"E30.0.3.11"),sQuery(id+"F4.wireOp",EDGE,"E30.0.3.12"),sQuery(id+"F4.wireOp",EDGE,"E30.0.3.13"),sQuery(id+"F4.wireOp",EDGE,"E30.0.4.0"),sQuery(id+"F4.wireOp",EDGE,"E30.0.4.1"),sQuery(id+"F4.wireOp",EDGE,"E30.0.4.2"),sQuery(id+"F4.wireOp",EDGE,"E30.0.4.3"),sQuery(id+"F4.wireOp",EDGE,"E30.0.4.4"),sQuery(id+"F4.wireOp",EDGE,"E30.0.4.5"),sQuery(id+"F4.wireOp",EDGE,"E30.0.4.6"),sQuery(id+"F4.wireOp",EDGE,"E30.0.4.7"),sQuery(id+"F4.wireOp",EDGE,"E30.0.4.8"),sQuery(id+"F4.wireOp",EDGE,"E30.0.4.9"),sQuery(id+"F4.wireOp",EDGE,"E30.0.4.10"),sQuery(id+"F4.wireOp",EDGE,"E30.0.4.11"),sQuery(id+"F4.wireOp",EDGE,"E30.0.4.12"),sQuery(id+"F4.wireOp",EDGE,"E30.0.4.13"),sQuery(id+"F4.wireOp",EDGE,"E30.0.5.0"),sQuery(id+"F4.wireOp",EDGE,"E30.0.5.1"),sQuery(id+"F4.wireOp",EDGE,"E30.0.5.2"),sQuery(id+"F4.wireOp",EDGE,"E30.0.5.3"),sQuery(id+"F4.wireOp",EDGE,"E30.0.5.4"),sQuery(id+"F4.wireOp",EDGE,"E30.0.5.5"),sQuery(id+"F4.wireOp",EDGE,"E30.0.5.6"),sQuery(id+"F4.wireOp",EDGE,"E30.0.5.7"),sQuery(id+"F4.wireOp",EDGE,"E30.0.5.8"),sQuery(id+"F4.wireOp",EDGE,"E30.0.5.9"),sQuery(id+"F4.wireOp",EDGE,"E30.0.5.10"),sQuery(id+"F4.wireOp",EDGE,"E30.0.5.11"),sQuery(id+"F4.wireOp",EDGE,"E30.0.5.12"),sQuery(id+"F4.wireOp",EDGE,"E30.0.5.13"),sQuery(id+"F4.wireOp",EDGE,"E31")])],"isStart":true})]});}
            var sketch = newSketch(context, id + "F8", { "sketchPlane" : qUnion([Q0])});
            skLineSegment(sketch, "E41", {"start": v(-304.8, 1752.6) * mm, "end": v(-304.8, 1727.2) * mm});
            skLineSegment(sketch, "E42", {"start": v(-304.8, 1727.2) * mm, "end": v(-330.2, 1727.2) * mm});
            skLineSegment(sketch, "E43", {"start": v(-330.2, 1727.2) * mm, "end": v(-330.2, 1714.5) * mm});
            skLineSegment(sketch, "E44", {"start": v(-330.2, 1714.5) * mm, "end": v(-266.7, 1714.5) * mm});
            skLineSegment(sketch, "E45", {"start": v(-266.7, 1714.5) * mm, "end": v(-266.7, 1727.2) * mm});
            skLineSegment(sketch, "E46", {"start": v(-266.7, 1727.2) * mm, "end": v(-292.1, 1727.2) * mm});
            skLineSegment(sketch, "E47", {"start": v(-292.1, 1727.2) * mm, "end": v(-292.1, 1752.6) * mm});
            skLineSegment(sketch, "E48", {"start": v(-304.8, 1752.6) * mm, "end": v(-292.1, 1752.6) * mm});
            skLineSegment(sketch, "E49", {"start": v(-374.65, 1727.2) * mm, "end": v(-349.25, 1727.2) * mm});
            skLineSegment(sketch, "E50", {"start": v(-349.25, 1727.2) * mm, "end": v(-349.25, 1714.5) * mm});
            skLineSegment(sketch, "E51", {"start": v(-349.25, 1714.5) * mm, "end": v(-374.65, 1714.5) * mm});
            skLineSegment(sketch, "E52.1.0.0", {"start": v(-247.65, 1714.5) * mm, "end": v(-184.15, 1714.5) * mm});
            skLineSegment(sketch, "E52.1.0.1", {"start": v(-247.65, 1727.2) * mm, "end": v(-247.65, 1714.5) * mm});
            skLineSegment(sketch, "E52.1.0.2", {"start": v(-222.25, 1727.2) * mm, "end": v(-247.65, 1727.2) * mm});
            skLineSegment(sketch, "E52.1.0.3", {"start": v(-222.25, 1752.6) * mm, "end": v(-222.25, 1727.2) * mm});
            skLineSegment(sketch, "E52.1.0.4", {"start": v(-209.55, 1727.2) * mm, "end": v(-209.55, 1752.6) * mm});
            skLineSegment(sketch, "E52.1.0.5", {"start": v(-222.25, 1752.6) * mm, "end": v(-209.55, 1752.6) * mm});
            skLineSegment(sketch, "E52.1.0.6", {"start": v(-184.15, 1727.2) * mm, "end": v(-209.55, 1727.2) * mm});
            skLineSegment(sketch, "E52.1.0.7", {"start": v(-184.15, 1714.5) * mm, "end": v(-184.15, 1727.2) * mm});
            skLineSegment(sketch, "E52.2.0.0", {"start": v(-165.1, 1714.5) * mm, "end": v(-101.6, 1714.5) * mm});
            skLineSegment(sketch, "E52.2.0.1", {"start": v(-165.1, 1727.2) * mm, "end": v(-165.1, 1714.5) * mm});
            skLineSegment(sketch, "E52.2.0.2", {"start": v(-139.7, 1727.2) * mm, "end": v(-165.1, 1727.2) * mm});
            skLineSegment(sketch, "E52.2.0.3", {"start": v(-139.7, 1752.6) * mm, "end": v(-139.7, 1727.2) * mm});
            skLineSegment(sketch, "E52.2.0.4", {"start": v(-127, 1727.2) * mm, "end": v(-127, 1752.6) * mm});
            skLineSegment(sketch, "E52.2.0.5", {"start": v(-139.7, 1752.6) * mm, "end": v(-127, 1752.6) * mm});
            skLineSegment(sketch, "E52.2.0.6", {"start": v(-101.6, 1727.2) * mm, "end": v(-127, 1727.2) * mm});
            skLineSegment(sketch, "E52.2.0.7", {"start": v(-101.6, 1714.5) * mm, "end": v(-101.6, 1727.2) * mm});
            skLineSegment(sketch, "E52.3.0.0", {"start": v(-82.55, 1714.5) * mm, "end": v(-19.05, 1714.5) * mm});
            skLineSegment(sketch, "E52.3.0.1", {"start": v(-82.55, 1727.2) * mm, "end": v(-82.55, 1714.5) * mm});
            skLineSegment(sketch, "E52.3.0.2", {"start": v(-57.15, 1727.2) * mm, "end": v(-82.55, 1727.2) * mm});
            skLineSegment(sketch, "E52.3.0.3", {"start": v(-57.15, 1752.6) * mm, "end": v(-57.15, 1727.2) * mm});
            skLineSegment(sketch, "E52.3.0.4", {"start": v(-44.45, 1727.2) * mm, "end": v(-44.45, 1752.6) * mm});
            skLineSegment(sketch, "E52.3.0.5", {"start": v(-57.15, 1752.6) * mm, "end": v(-44.45, 1752.6) * mm});
            skLineSegment(sketch, "E52.3.0.6", {"start": v(-19.05, 1727.2) * mm, "end": v(-44.45, 1727.2) * mm});
            skLineSegment(sketch, "E52.3.0.7", {"start": v(-19.05, 1714.5) * mm, "end": v(-19.05, 1727.2) * mm});
            skLineSegment(sketch, "E52.4.0.0", {"start": v(0, 1714.5) * mm, "end": v(63.5, 1714.5) * mm});
            skLineSegment(sketch, "E52.4.0.1", {"start": v(0, 1727.2) * mm, "end": v(0, 1714.5) * mm});
            skLineSegment(sketch, "E52.4.0.2", {"start": v(25.4, 1727.2) * mm, "end": v(0, 1727.2) * mm});
            skLineSegment(sketch, "E52.4.0.3", {"start": v(25.4, 1752.6) * mm, "end": v(25.4, 1727.2) * mm});
            skLineSegment(sketch, "E52.4.0.4", {"start": v(38.1, 1727.2) * mm, "end": v(38.1, 1752.6) * mm});
            skLineSegment(sketch, "E52.4.0.5", {"start": v(25.4, 1752.6) * mm, "end": v(38.1, 1752.6) * mm});
            skLineSegment(sketch, "E52.4.0.6", {"start": v(63.5, 1727.2) * mm, "end": v(38.1, 1727.2) * mm});
            skLineSegment(sketch, "E52.4.0.7", {"start": v(63.5, 1714.5) * mm, "end": v(63.5, 1727.2) * mm});
            skLineSegment(sketch, "E52.direction1", {"start": v(-330.2, 1714.5) * mm, "end": v(-247.65, 1714.5) * mm, "construction": true});
            skSolve(sketch);
        }
        {
            var Q0;
            Q0 = qSketchRegion(id + "F8", true);
            var Q1;
            {var subQ0=sQuery(id+"F8.wireOp",EDGE,"E49");Q1=makeQuery(id+"F8.imprint","IMPRINT",FACE,{"disambiguationData":[TD([[makeQuery(id+"F8.imprint","IMPRINT",EDGE,{"derivedFrom":subQ0}),-1.0]])]});}
            extrude(context, id + "F9", {"entities" : qUnion([Q0, Q1]), "operationType" : NewBodyOperationType.ADD, "endBound" : BoundingType.UP_TO_NEXT, "oppositeDirection" : true, "depth" : 83.31 * mm});
        }
        {
            var Q0;
            {var subQ0=sQuery(id+"F0.wireOp",EDGE,"E5.0");var subQ1=sQuery(id+"F0.wireOp",EDGE,"E5.2");Q0=makeQuery(id+"F9.boolean.opBoolean","MERGE",FACE,{"derivedFrom":[makeQuery(id+"F5.boolean.opBoolean","MERGE",FACE,{"derivedFrom":[makeQuery(id+"F1.opExtrude","CAP_FACE",FACE,{"disambiguationData":[OSD([sQuery(id+"F0.wireOp",EDGE,"E0"),sQuery(id+"F0.wireOp",EDGE,"E1"),sQuery(id+"F0.wireOp",EDGE,"E2"),sQuery(id+"F0.wireOp",EDGE,"E3"),sQuery(id+"F0.wireOp",EDGE,"E4.0"),subQ0,sQuery(id+"F0.wireOp",EDGE,"E5.1"),subQ1])],"isStart":true}),makeQuery(id+"F5.opExtrude","CAP_FACE",FACE,{"disambiguationData":[OSD([subQ0,subQ1,sQuery(id+"F4.wireOp",EDGE,"E9"),sQuery(id+"F4.wireOp",EDGE,"E10"),sQuery(id+"F4.wireOp",EDGE,"E11"),sQuery(id+"F4.wireOp",EDGE,"E12"),sQuery(id+"F4.wireOp",EDGE,"E13"),sQuery(id+"F4.wireOp",EDGE,"E14.0"),sQuery(id+"F4.wireOp",EDGE,"E15.1.0.0"),sQuery(id+"F4.wireOp",EDGE,"E15.1.0.1"),sQuery(id+"F4.wireOp",EDGE,"E15.2.0.0"),sQuery(id+"F4.wireOp",EDGE,"E15.2.0.1"),sQuery(id+"F4.wireOp",EDGE,"E15.3.0.0"),sQuery(id+"F4.wireOp",EDGE,"E15.3.0.1"),sQuery(id+"F4.wireOp",EDGE,"E15.4.0.0"),sQuery(id+"F4.wireOp",EDGE,"E15.4.0.1"),sQuery(id+"F4.wireOp",EDGE,"E15.5.0.0"),sQuery(id+"F4.wireOp",EDGE,"E15.5.0.1"),sQuery(id+"F4.wireOp",EDGE,"E16"),sQuery(id+"F4.wireOp",EDGE,"E17"),sQuery(id+"F4.wireOp",EDGE,"E18.trimOffspring"),sQuery(id+"F4.wireOp",EDGE,"E19.trimOffspring"),sQuery(id+"F4.wireOp",EDGE,"E20.trimOffspring"),sQuery(id+"F4.wireOp",EDGE,"E21.trimOffspring"),sQuery(id+"F4.wireOp",EDGE,"E22.trimOffspring"),sQuery(id+"F4.wireOp",EDGE,"E23"),sQuery(id+"F4.wireOp",EDGE,"E24.trimOffspring"),sQuery(id+"F4.wireOp",EDGE,"E25.trimOffspring"),sQuery(id+"F4.wireOp",EDGE,"E26.trimOffspring"),sQuery(id+"F4.wireOp",EDGE,"E27.trimOffspring"),sQuery(id+"F4.wireOp",EDGE,"E28.trimOffspring"),sQuery(id+"F4.wireOp",EDGE,"E29.trimOffspring"),sQuery(id+"F4.wireOp",EDGE,"E30.0.1.0"),sQuery(id+"F4.wireOp",EDGE,"E30.0.1.1"),sQuery(id+"F4.wireOp",EDGE,"E30.0.1.2"),sQuery(id+"F4.wireOp",EDGE,"E30.0.1.3"),sQuery(id+"F4.wireOp",EDGE,"E30.0.1.4"),sQuery(id+"F4.wireOp",EDGE,"E30.0.1.5"),sQuery(id+"F4.wireOp",EDGE,"E30.0.1.6"),sQuery(id+"F4.wireOp",EDGE,"E30.0.1.7"),sQuery(id+"F4.wireOp",EDGE,"E30.0.1.8"),sQuery(id+"F4.wireOp",EDGE,"E30.0.1.9"),sQuery(id+"F4.wireOp",EDGE,"E30.0.1.10"),sQuery(id+"F4.wireOp",EDGE,"E30.0.1.11"),sQuery(id+"F4.wireOp",EDGE,"E30.0.1.12"),sQuery(id+"F4.wireOp",EDGE,"E30.0.1.13"),sQuery(id+"F4.wireOp",EDGE,"E30.0.2.0"),sQuery(id+"F4.wireOp",EDGE,"E30.0.2.1"),sQuery(id+"F4.wireOp",EDGE,"E30.0.2.2"),sQuery(id+"F4.wireOp",EDGE,"E30.0.2.3"),sQuery(id+"F4.wireOp",EDGE,"E30.0.2.4"),sQuery(id+"F4.wireOp",EDGE,"E30.0.2.5"),sQuery(id+"F4.wireOp",EDGE,"E30.0.2.6"),sQuery(id+"F4.wireOp",EDGE,"E30.0.2.7"),sQuery(id+"F4.wireOp",EDGE,"E30.0.2.8"),sQuery(id+"F4.wireOp",EDGE,"E30.0.2.9"),sQuery(id+"F4.wireOp",EDGE,"E30.0.2.10"),sQuery(id+"F4.wireOp",EDGE,"E30.0.2.11"),sQuery(id+"F4.wireOp",EDGE,"E30.0.2.12"),sQuery(id+"F4.wireOp",EDGE,"E30.0.2.13"),sQuery(id+"F4.wireOp",EDGE,"E30.0.3.0"),sQuery(id+"F4.wireOp",EDGE,"E30.0.3.1"),sQuery(id+"F4.wireOp",EDGE,"E30.0.3.2"),sQuery(id+"F4.wireOp",EDGE,"E30.0.3.3"),sQuery(id+"F4.wireOp",EDGE,"E30.0.3.4"),sQuery(id+"F4.wireOp",EDGE,"E30.0.3.5"),sQuery(id+"F4.wireOp",EDGE,"E30.0.3.6"),sQuery(id+"F4.wireOp",EDGE,"E30.0.3.7"),sQuery(id+"F4.wireOp",EDGE,"E30.0.3.8"),sQuery(id+"F4.wireOp",EDGE,"E30.0.3.9"),sQuery(id+"F4.wireOp",EDGE,"E30.0.3.10"),sQuery(id+"F4.wireOp",EDGE,"E30.0.3.11"),sQuery(id+"F4.wireOp",EDGE,"E30.0.3.12"),sQuery(id+"F4.wireOp",EDGE,"E30.0.3.13"),sQuery(id+"F4.wireOp",EDGE,"E30.0.4.0"),sQuery(id+"F4.wireOp",EDGE,"E30.0.4.1"),sQuery(id+"F4.wireOp",EDGE,"E30.0.4.2"),sQuery(id+"F4.wireOp",EDGE,"E30.0.4.3"),sQuery(id+"F4.wireOp",EDGE,"E30.0.4.4"),sQuery(id+"F4.wireOp",EDGE,"E30.0.4.5"),sQuery(id+"F4.wireOp",EDGE,"E30.0.4.6"),sQuery(id+"F4.wireOp",EDGE,"E30.0.4.7"),sQuery(id+"F4.wireOp",EDGE,"E30.0.4.8"),sQuery(id+"F4.wireOp",EDGE,"E30.0.4.9"),sQuery(id+"F4.wireOp",EDGE,"E30.0.4.10"),sQuery(id+"F4.wireOp",EDGE,"E30.0.4.11"),sQuery(id+"F4.wireOp",EDGE,"E30.0.4.12"),sQuery(id+"F4.wireOp",EDGE,"E30.0.4.13"),sQuery(id+"F4.wireOp",EDGE,"E30.0.5.0"),sQuery(id+"F4.wireOp",EDGE,"E30.0.5.1"),sQuery(id+"F4.wireOp",EDGE,"E30.0.5.2"),sQuery(id+"F4.wireOp",EDGE,"E30.0.5.3"),sQuery(id+"F4.wireOp",EDGE,"E30.0.5.4"),sQuery(id+"F4.wireOp",EDGE,"E30.0.5.5"),sQuery(id+"F4.wireOp",EDGE,"E30.0.5.6"),sQuery(id+"F4.wireOp",EDGE,"E30.0.5.7"),sQuery(id+"F4.wireOp",EDGE,"E30.0.5.8"),sQuery(id+"F4.wireOp",EDGE,"E30.0.5.9"),sQuery(id+"F4.wireOp",EDGE,"E30.0.5.10"),sQuery(id+"F4.wireOp",EDGE,"E30.0.5.11"),sQuery(id+"F4.wireOp",EDGE,"E30.0.5.12"),sQuery(id+"F4.wireOp",EDGE,"E30.0.5.13"),sQuery(id+"F4.wireOp",EDGE,"E31")])],"isStart":true})]}),makeQuery(id+"F9.opExtrude","CAP_FACE",FACE,{"disambiguationData":[OSD([sQuery(id+"F8.wireOp",EDGE,"E41"),sQuery(id+"F8.wireOp",EDGE,"E42"),sQuery(id+"F8.wireOp",EDGE,"E43"),sQuery(id+"F8.wireOp",EDGE,"E44"),sQuery(id+"F8.wireOp",EDGE,"E45"),sQuery(id+"F8.wireOp",EDGE,"E46"),sQuery(id+"F8.wireOp",EDGE,"E47"),sQuery(id+"F8.wireOp",EDGE,"E48")])],"isStart":true}),makeQuery(id+"F9.opExtrude","CAP_FACE",FACE,{"disambiguationData":[OSD([subQ0,sQuery(id+"F8.wireOp",EDGE,"E49"),sQuery(id+"F8.wireOp",EDGE,"E50"),sQuery(id+"F8.wireOp",EDGE,"E51")])],"isStart":true}),makeQuery(id+"F9.opExtrude","CAP_FACE",FACE,{"disambiguationData":[OSD([sQuery(id+"F8.wireOp",EDGE,"E52.1.0.0"),sQuery(id+"F8.wireOp",EDGE,"E52.1.0.1"),sQuery(id+"F8.wireOp",EDGE,"E52.1.0.2"),sQuery(id+"F8.wireOp",EDGE,"E52.1.0.3"),sQuery(id+"F8.wireOp",EDGE,"E52.1.0.4"),sQuery(id+"F8.wireOp",EDGE,"E52.1.0.5"),sQuery(id+"F8.wireOp",EDGE,"E52.1.0.6"),sQuery(id+"F8.wireOp",EDGE,"E52.1.0.7")])],"isStart":true}),makeQuery(id+"F9.opExtrude","CAP_FACE",FACE,{"disambiguationData":[OSD([sQuery(id+"F8.wireOp",EDGE,"E52.2.0.0"),sQuery(id+"F8.wireOp",EDGE,"E52.2.0.1"),sQuery(id+"F8.wireOp",EDGE,"E52.2.0.2"),sQuery(id+"F8.wireOp",EDGE,"E52.2.0.3"),sQuery(id+"F8.wireOp",EDGE,"E52.2.0.4"),sQuery(id+"F8.wireOp",EDGE,"E52.2.0.5"),sQuery(id+"F8.wireOp",EDGE,"E52.2.0.6"),sQuery(id+"F8.wireOp",EDGE,"E52.2.0.7")])],"isStart":true}),makeQuery(id+"F9.opExtrude","CAP_FACE",FACE,{"disambiguationData":[OSD([sQuery(id+"F8.wireOp",EDGE,"E52.3.0.0"),sQuery(id+"F8.wireOp",EDGE,"E52.3.0.1"),sQuery(id+"F8.wireOp",EDGE,"E52.3.0.2"),sQuery(id+"F8.wireOp",EDGE,"E52.3.0.3"),sQuery(id+"F8.wireOp",EDGE,"E52.3.0.4"),sQuery(id+"F8.wireOp",EDGE,"E52.3.0.5"),sQuery(id+"F8.wireOp",EDGE,"E52.3.0.6"),sQuery(id+"F8.wireOp",EDGE,"E52.3.0.7")])],"isStart":true}),makeQuery(id+"F9.opExtrude","CAP_FACE",FACE,{"disambiguationData":[OSD([sQuery(id+"F8.wireOp",EDGE,"E52.4.0.0"),sQuery(id+"F8.wireOp",EDGE,"E52.4.0.1"),sQuery(id+"F8.wireOp",EDGE,"E52.4.0.2"),sQuery(id+"F8.wireOp",EDGE,"E52.4.0.3"),sQuery(id+"F8.wireOp",EDGE,"E52.4.0.4"),sQuery(id+"F8.wireOp",EDGE,"E52.4.0.5"),sQuery(id+"F8.wireOp",EDGE,"E52.4.0.6"),sQuery(id+"F8.wireOp",EDGE,"E52.4.0.7")])],"isStart":true})]});}
            var sketch = newSketch(context, id + "F10", { "sketchPlane" : qUnion([Q0])});
            skLineSegment(sketch, "E53", {"start": v(374.65, 1409.7) * mm, "end": v(107.95, 1409.7) * mm});
            skLineSegment(sketch, "E54", {"start": v(107.95, 1409.7) * mm, "end": v(107.95, 1714.5) * mm});
            skLineSegment(sketch, "E55.0", {"start": v(120.65, 1422.4) * mm, "end": v(120.65, 1752.6) * mm});
            skLineSegment(sketch, "E55.1", {"start": v(374.65, 1422.4) * mm, "end": v(120.65, 1422.4) * mm});
            skLineSegment(sketch, "E56", {"start": v(120.65, 1752.6) * mm, "end": v(107.95, 1752.6) * mm});
            skLineSegment(sketch, "E57", {"start": v(374.65, 1422.4) * mm, "end": v(374.65, 1409.7) * mm});
            skLineSegment(sketch, "E58", {"start": v(107.95, 1727.2) * mm, "end": v(82.55, 1727.2) * mm});
            skLineSegment(sketch, "E59", {"start": v(82.55, 1727.2) * mm, "end": v(82.55, 1714.5) * mm});
            skLineSegment(sketch, "E60", {"start": v(82.55, 1714.5) * mm, "end": v(107.95, 1714.5) * mm});
            skLineSegment(sketch, "E61.trimOffspring", {"start": v(107.95, 1727.2) * mm, "end": v(107.95, 1752.6) * mm});
            skSolve(sketch);
        }
        {
            var Q0;
            Q0 = qSketchRegion(id + "F10", true);
            extrude(context, id + "F11", {"entities" : qUnion([Q0]), "operationType" : NewBodyOperationType.ADD, "endBound" : BoundingType.UP_TO_NEXT, "oppositeDirection" : true, "depth" : 45.72 * mm});
        }
    });
